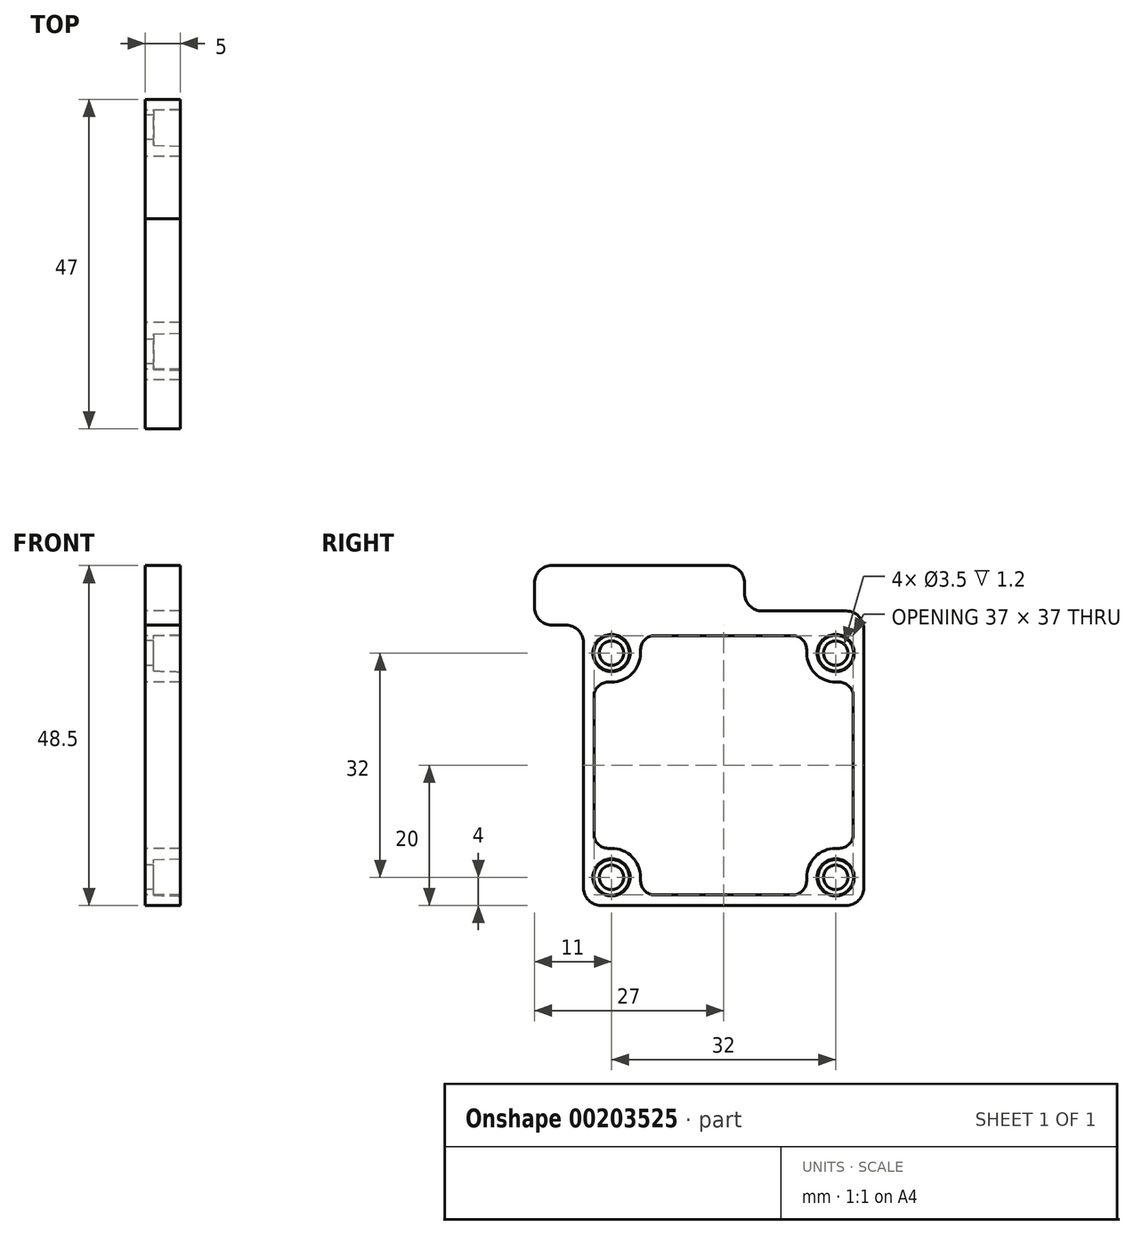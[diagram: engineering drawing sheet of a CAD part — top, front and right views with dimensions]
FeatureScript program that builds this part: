
annotation { "Feature Type Name" : "Feature", "Feature Type Description" : "" }
export const myFeature = defineFeature(function(context is Context, id is Id, definition is map)
    precondition{}
    {
        {
            var Q0;
            Q0=qCreatedBy(makeId("Right.planeOp"),FACE);
            var sketch = newSketch(context, id + "F0", { "sketchPlane" : qUnion([Q0])});
            skPoint(sketch, "E0.middle", {"position": v(0, 0) * mm});
            skPoint(sketch, "E1", {"position": v(16, 0) * mm});
            skCircle(sketch, "E2", {"center": v(-16, 16) * mm, "radius": 2.15 * mm});
            skCircle(sketch, "E3", {"center": v(16, 16) * mm, "radius": 2.15 * mm});
            skCircle(sketch, "E4", {"center": v(16, -16) * mm, "radius": 2.15 * mm});
            skCircle(sketch, "E5", {"center": v(-16, -16) * mm, "radius": 2.15 * mm});
            skArc(sketch, "E6.0", {"start": v(11.85, 16) * mm, "mid": v(13.07, 13.07) * mm, "end": v(16, 11.85) * mm});
            skArc(sketch, "E7.0", {"start": v(16, -11.85) * mm, "mid": v(13.07, -13.07) * mm, "end": v(11.85, -16) * mm});
            skLineSegment(sketch, "E8.bottom", {"start": v(20, -20) * mm, "end": v(-20, -20) * mm});
            skLineSegment(sketch, "E8.top", {"start": v(20, 20) * mm, "end": v(-20, 20) * mm});
            skLineSegment(sketch, "E8.left", {"start": v(20, -20) * mm, "end": v(20, 20) * mm});
            skLineSegment(sketch, "E8.right", {"start": v(-20, -20) * mm, "end": v(-20, 20) * mm});
            skLineSegment(sketch, "E9.left", {"start": v(-20, 20) * mm, "end": v(-20, 20) * mm});
            skLineSegment(sketch, "E9.right", {"start": v(20, 20) * mm, "end": v(20, 20) * mm});
            skLineSegment(sketch, "E10.top", {"start": v(-20, 22) * mm, "end": v(20, 22) * mm});
            skLineSegment(sketch, "E10.left", {"start": v(-20, 20) * mm, "end": v(-20, 22) * mm});
            skLineSegment(sketch, "E10.right", {"start": v(20, 20) * mm, "end": v(20, 22) * mm});
            skLineSegment(sketch, "E11", {"start": v(-18.5, 9.85) * mm, "end": v(-18.5, -9.85) * mm});
            skLineSegment(sketch, "E12", {"start": v(-9.85, 18.5) * mm, "end": v(9.85, 18.5) * mm});
            skLineSegment(sketch, "E13", {"start": v(18.5, 9.85) * mm, "end": v(18.5, -9.85) * mm});
            skLineSegment(sketch, "E14", {"start": v(-9.85, -18.5) * mm, "end": v(9.85, -18.5) * mm});
            skLineSegment(sketch, "E15", {"start": v(-11.85, 16) * mm, "end": v(-11.85, 16.5) * mm});
            skLineSegment(sketch, "E16", {"start": v(11.85, 16) * mm, "end": v(11.85, 16.5) * mm});
            skLineSegment(sketch, "E17", {"start": v(16, 11.85) * mm, "end": v(16.5, 11.85) * mm});
            skLineSegment(sketch, "E18", {"start": v(16, -11.85) * mm, "end": v(16.5, -11.85) * mm});
            skLineSegment(sketch, "E19", {"start": v(11.85, -16) * mm, "end": v(11.85, -16.5) * mm});
            skLineSegment(sketch, "E20", {"start": v(-11.85, -16) * mm, "end": v(-11.85, -16.5) * mm});
            skLineSegment(sketch, "E21", {"start": v(-16, -11.85) * mm, "end": v(-16.5, -11.85) * mm});
            skArc(sketch, "E22.trimOffspring", {"start": v(-11.85, -16) * mm, "mid": v(-13.07, -13.07) * mm, "end": v(-16, -11.85) * mm});
            skLineSegment(sketch, "E23", {"start": v(-16, 11.85) * mm, "end": v(-16.5, 11.85) * mm});
            skArc(sketch, "E24.trimOffspring", {"start": v(-16, 11.85) * mm, "mid": v(-13.07, 13.07) * mm, "end": v(-11.85, 16) * mm});
            skPoint(sketch, "E25.visualSharp", {"position": v(-11.85, 18.5) * mm});
            skArc(sketch, "E25.filletArc", {"start": v(-9.85, 18.5) * mm, "mid": v(-11.26, 17.91) * mm, "end": v(-11.85, 16.5) * mm});
            skPoint(sketch, "E26.visualSharp", {"position": v(11.85, 18.5) * mm});
            skArc(sketch, "E26.filletArc", {"start": v(11.85, 16.5) * mm, "mid": v(11.26, 17.91) * mm, "end": v(9.85, 18.5) * mm});
            skPoint(sketch, "E27.visualSharp", {"position": v(18.5, 11.85) * mm});
            skArc(sketch, "E27.filletArc", {"start": v(18.5, 9.85) * mm, "mid": v(17.91, 11.26) * mm, "end": v(16.5, 11.85) * mm});
            skPoint(sketch, "E28.visualSharp", {"position": v(18.5, -11.85) * mm});
            skArc(sketch, "E28.filletArc", {"start": v(16.5, -11.85) * mm, "mid": v(17.91, -11.26) * mm, "end": v(18.5, -9.85) * mm});
            skPoint(sketch, "E29.visualSharp", {"position": v(11.85, -18.5) * mm});
            skArc(sketch, "E29.filletArc", {"start": v(9.85, -18.5) * mm, "mid": v(11.26, -17.91) * mm, "end": v(11.85, -16.5) * mm});
            skPoint(sketch, "E30.visualSharp", {"position": v(-11.85, -18.5) * mm});
            skArc(sketch, "E30.filletArc", {"start": v(-11.85, -16.5) * mm, "mid": v(-11.26, -17.91) * mm, "end": v(-9.85, -18.5) * mm});
            skPoint(sketch, "E31.visualSharp", {"position": v(-18.5, -11.85) * mm});
            skArc(sketch, "E31.filletArc", {"start": v(-18.5, -9.85) * mm, "mid": v(-17.91, -11.26) * mm, "end": v(-16.5, -11.85) * mm});
            skPoint(sketch, "E32.visualSharp", {"position": v(-18.5, 11.85) * mm});
            skArc(sketch, "E32.filletArc", {"start": v(-16.5, 11.85) * mm, "mid": v(-17.91, 11.26) * mm, "end": v(-18.5, 9.85) * mm});
            skLineSegment(sketch, "E33.bottom", {"start": v(3, 20) * mm, "end": v(-27, 20) * mm});
            skLineSegment(sketch, "E33.top", {"start": v(3, 28.5) * mm, "end": v(-27, 28.5) * mm});
            skLineSegment(sketch, "E33.left", {"start": v(3, 20) * mm, "end": v(3, 28.5) * mm});
            skLineSegment(sketch, "E33.right", {"start": v(-27, 20) * mm, "end": v(-27, 28.5) * mm});
            skSolve(sketch);
        }
        {
            var Q0;
            Q0=qSketchRegion(id+"F0",true);
            var Q1;
            Q1=makeQuery(id+"F0.imprint","IMPRINT",FACE,{"disambiguationData":[TD([[makeQuery(id+"F0.imprint","IMPRINT",EDGE,{"derivedFrom":sQuery(id+"F0.wireOp",EDGE,"E2")}),1.0]])]});
            var Q2;
            Q2=makeQuery(id+"F0.imprint","IMPRINT",FACE,{"disambiguationData":[TD([[makeQuery(id+"F0.imprint","IMPRINT",EDGE,{"derivedFrom":sQuery(id+"F0.wireOp",EDGE,"E3")}),1.0]])]});
            var Q3;
            Q3=makeQuery(id+"F0.imprint","IMPRINT",FACE,{"disambiguationData":[TD([[makeQuery(id+"F0.imprint","IMPRINT",EDGE,{"derivedFrom":sQuery(id+"F0.wireOp",EDGE,"E5")}),1.0]])]});
            var Q4;
            Q4=makeQuery(id+"F0.imprint","IMPRINT",FACE,{"disambiguationData":[TD([[makeQuery(id+"F0.imprint","IMPRINT",EDGE,{"derivedFrom":sQuery(id+"F0.wireOp",EDGE,"E4")}),1.0]])]});
            extrude(context, id + "F1", {"entities" : qUnion([Q0, Q1, Q2, Q3, Q4]), "depth" : 5 * mm});
        }
        {
            var Q0;
            Q0=makeQuery(id+"F1.opExtrude","CAP_FACE",FACE,{"disambiguationData":[OSD([sQuery(id+"F0.wireOp",EDGE,"E6.0"),sQuery(id+"F0.wireOp",EDGE,"E7.0"),sQuery(id+"F0.wireOp",EDGE,"E8.bottom"),sQuery(id+"F0.wireOp",EDGE,"E8.left"),sQuery(id+"F0.wireOp",EDGE,"E8.right"),sQuery(id+"F0.wireOp",EDGE,"E10.top"),sQuery(id+"F0.wireOp",EDGE,"E10.right"),sQuery(id+"F0.wireOp",EDGE,"E11"),sQuery(id+"F0.wireOp",EDGE,"E12"),sQuery(id+"F0.wireOp",EDGE,"E13"),sQuery(id+"F0.wireOp",EDGE,"E14"),sQuery(id+"F0.wireOp",EDGE,"E15"),sQuery(id+"F0.wireOp",EDGE,"E16"),sQuery(id+"F0.wireOp",EDGE,"E17"),sQuery(id+"F0.wireOp",EDGE,"E18"),sQuery(id+"F0.wireOp",EDGE,"E19"),sQuery(id+"F0.wireOp",EDGE,"E20"),sQuery(id+"F0.wireOp",EDGE,"E21"),sQuery(id+"F0.wireOp",EDGE,"E22.trimOffspring"),sQuery(id+"F0.wireOp",EDGE,"E23"),sQuery(id+"F0.wireOp",EDGE,"E24.trimOffspring"),sQuery(id+"F0.wireOp",EDGE,"E25.filletArc"),sQuery(id+"F0.wireOp",EDGE,"E26.filletArc"),sQuery(id+"F0.wireOp",EDGE,"E27.filletArc"),sQuery(id+"F0.wireOp",EDGE,"E28.filletArc"),sQuery(id+"F0.wireOp",EDGE,"E29.filletArc"),sQuery(id+"F0.wireOp",EDGE,"E30.filletArc"),sQuery(id+"F0.wireOp",EDGE,"E31.filletArc"),sQuery(id+"F0.wireOp",EDGE,"E32.filletArc"),sQuery(id+"F0.wireOp",EDGE,"E33.bottom"),sQuery(id+"F0.wireOp",EDGE,"E33.top"),sQuery(id+"F0.wireOp",EDGE,"E33.left"),sQuery(id+"F0.wireOp",EDGE,"E33.right")])],"isStart":false});
            var sketch = newSketch(context, id + "F2", { "sketchPlane" : qUnion([Q0])});
            skPoint(sketch, "E34", {"position": v(-16, 16) * mm});
            skPoint(sketch, "E35", {"position": v(16, 16) * mm});
            skPoint(sketch, "E36", {"position": v(16, -16) * mm});
            skPoint(sketch, "E37", {"position": v(-16, -16) * mm});
            skCircle(sketch, "E38", {"center": v(-16, 16) * mm, "radius": 2.65 * mm});
            skCircle(sketch, "E39", {"center": v(16, 16) * mm, "radius": 2.65 * mm});
            skCircle(sketch, "E40", {"center": v(16, -16) * mm, "radius": 2.65 * mm});
            skCircle(sketch, "E41", {"center": v(-16, -16) * mm, "radius": 2.65 * mm});
            skSolve(sketch);
        }
        {
            var Q0;
            Q0=qSketchRegion(id+"F2",true);
            extrude(context, id + "F3", {"entities" : qUnion([Q0]), "operationType" : NewBodyOperationType.REMOVE, "oppositeDirection" : true, "depth" : 3.8 * mm, "hasDraft" : true, "draftAngle" : 1.5 * degree, "draftPullDirection" : true});
        }
        {
            var Q0;
            Q0=sQuery(id+"F0.wireOp",VERTEX,"E2.center");
            var Q1;
            Q1=sQuery(id+"F0.wireOp",VERTEX,"E3.center");
            var Q2;
            Q2=sQuery(id+"F0.wireOp",VERTEX,"E4.center");
            var Q3;
            Q3=sQuery(id+"F0.wireOp",VERTEX,"E5.center");
            var Q4;
            Q4=makeQuery(id+"F1.opExtrude","SWEPT_BODY",BODY,{"disambiguationData":[OSD([sQuery(id+"F0.wireOp",EDGE,"E6.0"),sQuery(id+"F0.wireOp",EDGE,"E7.0"),sQuery(id+"F0.wireOp",EDGE,"E8.bottom"),sQuery(id+"F0.wireOp",EDGE,"E8.left"),sQuery(id+"F0.wireOp",EDGE,"E8.right"),sQuery(id+"F0.wireOp",EDGE,"E10.top"),sQuery(id+"F0.wireOp",EDGE,"E10.right"),sQuery(id+"F0.wireOp",EDGE,"E11"),sQuery(id+"F0.wireOp",EDGE,"E12"),sQuery(id+"F0.wireOp",EDGE,"E13"),sQuery(id+"F0.wireOp",EDGE,"E14"),sQuery(id+"F0.wireOp",EDGE,"E15"),sQuery(id+"F0.wireOp",EDGE,"E16"),sQuery(id+"F0.wireOp",EDGE,"E17"),sQuery(id+"F0.wireOp",EDGE,"E18"),sQuery(id+"F0.wireOp",EDGE,"E19"),sQuery(id+"F0.wireOp",EDGE,"E20"),sQuery(id+"F0.wireOp",EDGE,"E21"),sQuery(id+"F0.wireOp",EDGE,"E22.trimOffspring"),sQuery(id+"F0.wireOp",EDGE,"E23"),sQuery(id+"F0.wireOp",EDGE,"E24.trimOffspring"),sQuery(id+"F0.wireOp",EDGE,"E25.filletArc"),sQuery(id+"F0.wireOp",EDGE,"E26.filletArc"),sQuery(id+"F0.wireOp",EDGE,"E27.filletArc"),sQuery(id+"F0.wireOp",EDGE,"E28.filletArc"),sQuery(id+"F0.wireOp",EDGE,"E29.filletArc"),sQuery(id+"F0.wireOp",EDGE,"E30.filletArc"),sQuery(id+"F0.wireOp",EDGE,"E31.filletArc"),sQuery(id+"F0.wireOp",EDGE,"E32.filletArc"),sQuery(id+"F0.wireOp",EDGE,"E33.bottom"),sQuery(id+"F0.wireOp",EDGE,"E33.top"),sQuery(id+"F0.wireOp",EDGE,"E33.left"),sQuery(id+"F0.wireOp",EDGE,"E33.right")])]});
            hole(context, id + "F4", {"style" : HoleStyle.SIMPLE, "endStyle" : HoleEndStyle.THROUGH, "oppositeDirection" : true, "holeDiameter" : 3.5 * mm, "startFromSketch" : true, "locations" : qUnion([Q0, Q1, Q2, Q3]), "scope" : qUnion([Q4]), "isTappedThrough" : true});
        }
        {
            var Q0;
            Q0=makeQuery(id+"F1.opExtrude","SWEPT_EDGE",EDGE,{"disambiguationData":[OSD([sQuery(id+"F0.wireOp",EDGE,"E10.top"),sQuery(id+"F0.wireOp",EDGE,"E33.left")])]});
            var Q1;
            Q1=makeQuery(id+"F1.opExtrude","SWEPT_EDGE",EDGE,{"disambiguationData":[OSD([sQuery(id+"F0.wireOp",EDGE,"E33.top"),sQuery(id+"F0.wireOp",EDGE,"E33.left")])]});
            var Q2;
            Q2=makeQuery(id+"F1.opExtrude","SWEPT_EDGE",EDGE,{"disambiguationData":[OSD([sQuery(id+"F0.wireOp",EDGE,"E10.top"),sQuery(id+"F0.wireOp",EDGE,"E10.right")])]});
            var Q3;
            Q3=makeQuery(id+"F1.opExtrude","SWEPT_EDGE",EDGE,{"disambiguationData":[OSD([sQuery(id+"F0.wireOp",EDGE,"E8.bottom"),sQuery(id+"F0.wireOp",EDGE,"E8.left")])]});
            var Q4;
            Q4=makeQuery(id+"F1.opExtrude","SWEPT_EDGE",EDGE,{"disambiguationData":[OSD([sQuery(id+"F0.wireOp",EDGE,"E8.bottom"),sQuery(id+"F0.wireOp",EDGE,"E8.right")])]});
            var Q5;
            Q5=makeQuery(id+"F1.opExtrude","SWEPT_EDGE",EDGE,{"disambiguationData":[OSD([sQuery(id+"F0.wireOp",EDGE,"E8.right"),sQuery(id+"F0.wireOp",EDGE,"E10.left"),sQuery(id+"F0.wireOp",EDGE,"E33.bottom")])]});
            var Q6;
            Q6=makeQuery(id+"F1.opExtrude","SWEPT_EDGE",EDGE,{"disambiguationData":[OSD([sQuery(id+"F0.wireOp",EDGE,"E33.bottom"),sQuery(id+"F0.wireOp",EDGE,"E33.right")])]});
            var Q7;
            Q7=makeQuery(id+"F1.opExtrude","SWEPT_EDGE",EDGE,{"disambiguationData":[OSD([sQuery(id+"F0.wireOp",EDGE,"E33.top"),sQuery(id+"F0.wireOp",EDGE,"E33.right")])]});
            fillet(context, id + "F5", {"entities" : qUnion([Q0, Q1, Q2, Q3, Q4, Q5, Q6, Q7]), "radius" : 2.5 * mm, "tangentPropagation" : true, "allowEdgeOverflow" : false});
        }
    });
